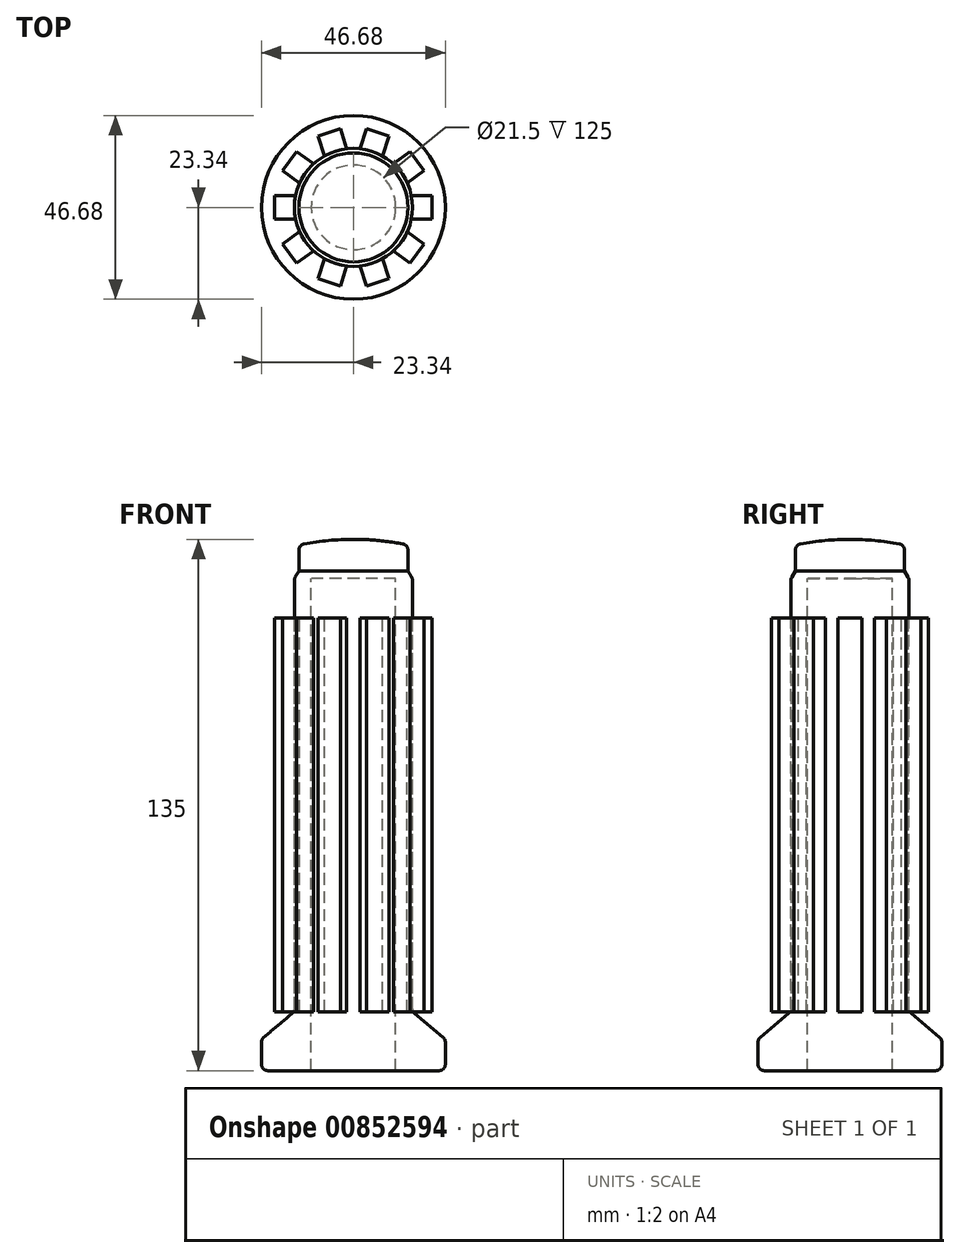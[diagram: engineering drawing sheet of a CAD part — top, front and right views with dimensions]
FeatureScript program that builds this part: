
annotation { "Feature Type Name" : "Feature", "Feature Type Description" : "" }
export const myFeature = defineFeature(function(context is Context, id is Id, definition is map)
    precondition{}
    {
        {
            var Q0;
            Q0=qCreatedBy(makeId("Front.planeOp"),FACE);
            var sketch = newSketch(context, id + "F0", { "sketchPlane" : qUnion([Q0])});
            skLineSegment(sketch, "E0", {"start": v(0, 5.97) * mm, "end": v(0, 0) * mm, "construction": true});
            skLineSegment(sketch, "E1", {"start": v(0, 135) * mm, "end": v(0, 125) * mm});
            skLineSegment(sketch, "E2", {"start": v(0, 125) * mm, "end": v(10.75, 125) * mm});
            skLineSegment(sketch, "E3", {"start": v(10.75, 125) * mm, "end": v(10.75, 0) * mm});
            skLineSegment(sketch, "E4", {"start": v(10.75, 0) * mm, "end": v(23.34, 0) * mm});
            skLineSegment(sketch, "E5", {"start": v(23.34, 0) * mm, "end": v(23.34, 8) * mm});
            skLineSegment(sketch, "E6", {"start": v(23.34, 8) * mm, "end": v(15, 15) * mm});
            skLineSegment(sketch, "E7", {"start": v(15, 15) * mm, "end": v(15, 125) * mm});
            skLineSegment(sketch, "E8", {"start": v(15, 125) * mm, "end": v(13.85, 127) * mm});
            skLineSegment(sketch, "E9", {"start": v(13.85, 127) * mm, "end": v(13.85, 133.58) * mm});
            skArc(sketch, "E10", {"start": v(13.85, 133.58) * mm, "mid": v(6.96, 134.64) * mm, "end": v(0, 135) * mm});
            skSolve(sketch);
        }
        {
            var Q0;
            Q0=makeQuery(id+"F0.imprint","IMPRINT",FACE,{"disambiguationData":[TD([[makeQuery(id+"F0.imprint","IMPRINT",EDGE,{"derivedFrom":sQuery(id+"F0.wireOp",EDGE,"E1")}),1.0]])]});
            var Q1;
            Q1=sQuery(id+"F0.wireOp",EDGE,"E0");
            revolve(context, id + "F1", {"surfaceOperationType" : NewSurfaceOperationType.NEW, "entities" : qUnion([Q0]), "axis" : qUnion([Q1]), "revolveType" : RevolveType.FULL});
        }
        {
            var Q0;
            Q0=makeQuery(id+"F1.opRevolve","SWEPT_EDGE",EDGE,{"disambiguationData":[OSD([sQuery(id+"F0.wireOp",EDGE,"E9"),sQuery(id+"F0.wireOp",EDGE,"E10")])]});
            var Q1;
            Q1=makeQuery(id+"F1.opRevolve","SWEPT_EDGE",EDGE,{"disambiguationData":[OSD([sQuery(id+"F0.wireOp",EDGE,"E7"),sQuery(id+"F0.wireOp",EDGE,"E8")])]});
            var Q2;
            Q2=makeQuery(id+"F1.opRevolve","SWEPT_EDGE",EDGE,{"disambiguationData":[OSD([sQuery(id+"F0.wireOp",EDGE,"E5"),sQuery(id+"F0.wireOp",EDGE,"E6")])]});
            var Q3;
            Q3=makeQuery(id+"F1.opRevolve","SWEPT_EDGE",EDGE,{"disambiguationData":[OSD([sQuery(id+"F0.wireOp",EDGE,"E4"),sQuery(id+"F0.wireOp",EDGE,"E5")])]});
            var Q4;
            Q4=makeQuery(id+"F1.opRevolve","SWEPT_EDGE",EDGE,{"disambiguationData":[OSD([sQuery(id+"F0.wireOp",EDGE,"E6"),sQuery(id+"F0.wireOp",EDGE,"E7")])]});
            fillet(context, id + "F2", {"entities" : qUnion([Q0, Q1, Q2, Q3, Q4]), "radius" : 1.6 * mm, "tangentPropagation" : true, "allowEdgeOverflow" : false});
        }
        {
            var Q0;
            Q0=qCreatedBy(makeId("Right.planeOp"),FACE);
            cPlane(context, id + "F3", {"entities" : qUnion([Q0]), "cplaneType" : CPlaneType.OFFSET, "offset" : 20 * mm, "width" : 150 * mm, "height" : 150 * mm});
        }
        {
            var Q0;
            Q0=qCreatedBy(id+"F3.planeOp",FACE);
            var sketch = newSketch(context, id + "F4", { "sketchPlane" : qUnion([Q0])});
            skLineSegment(sketch, "E11.bottom", {"start": v(-3, 115) * mm, "end": v(3, 115) * mm});
            skLineSegment(sketch, "E11.top", {"start": v(-3, 15) * mm, "end": v(3, 15) * mm});
            skLineSegment(sketch, "E11.left", {"start": v(-3, 115) * mm, "end": v(-3, 15) * mm});
            skLineSegment(sketch, "E11.right", {"start": v(3, 115) * mm, "end": v(3, 15) * mm});
            skSolve(sketch);
        }
        {
            var Q0;
            Q0 = qSketchRegion(id + "F4", true);
            var Q1;
            Q1=makeQuery(id+"F1.opRevolve","SWEPT_FACE",FACE,{"disambiguationData":[OSD([sQuery(id+"F0.wireOp",EDGE,"E7")])]});
            extrude(context, id + "F5", {"entities" : qUnion([Q0]), "endBound" : BoundingType.UP_TO_SURFACE, "oppositeDirection" : true, "depth" : 25 * mm, "endBoundEntityFace" : qUnion([Q1]), "offsetDistance" : 25 * mm});
        }
        {
            var Q0;
            Q0=makeQuery(id+"F5.opExtrude","SWEPT_BODY",BODY,{"disambiguationData":[OSD([sQuery(id+"F4.wireOp",EDGE,"E11.bottom"),sQuery(id+"F4.wireOp",EDGE,"E11.top"),sQuery(id+"F4.wireOp",EDGE,"E11.left"),sQuery(id+"F4.wireOp",EDGE,"E11.right")])]});
            var Q1;
            Q1=makeQuery(id+"F1.opRevolve","SWEPT_FACE",FACE,{"disambiguationData":[OSD([sQuery(id+"F0.wireOp",EDGE,"E7")])]});
            circularPattern(context, id + "F6", {"entities" : qUnion([Q0]), "axis" : qUnion([Q1]), "angle" : 360 * degree, "instanceCount" : 10, "equalSpace" : true});
        }
    });
